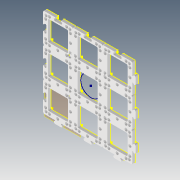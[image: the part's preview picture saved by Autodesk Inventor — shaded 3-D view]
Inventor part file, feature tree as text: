
AUTODESK INVENTOR PART (.ipt)
format: ipt  version: 2022 (Build 260153000, 153)  size: 1,184,256 bytes
history: native  units: mm
features: other x5, sketch x4, extrude x2, reference x2, projected_geometry x2, plane x1, pattern_linear x1, hole x1
ambient origin geometry x8: Origin, YZ Plane, XZ Plane, XY Plane, X Axis, Y Axis, Z Axis, Center Point
bodies: Solid2 (feature_tree)
feature tree (18):
  plane  "Work Plane2"
  extrude  "Extrusion2"  Depth=5.0mm
  pattern_linear  "Rectangular Pattern1"  Spacing1=0.05mm  [1 undecoded]
  extrude  "Extrusion3"  Depth=20.594885mm
  hole  "Hole2"  [1 undecoded]
  sketch  "Skizze6"  dims[d26=0.05mm d27=0.05mm d28=0.05mm d29=0.05mm d30=0.05mm d31=30.0mm d33=50.0mm d34=30.0mm d36=50.0mm d37=5.0mm d38=0.0mm d39=60.0mm d40=60.0mm d41=3.0mm d42=6.0mm d43=6.0mm d44=3.0mm d45=90.0deg d46=8.0mm d47=20.594885mm]
  sketch  "Sketch3"  dims[d21=5.0mm d22=0.0mm d23=0.05mm]
  reference  "Reference47"
  sketch  "Sketch4"  dims[d24=0.05mm]
  projected_geometry  "Projected Loop1"
  sketch  "Sketch5"  dims[d25=0.05mm]
  reference  "Reference48"
  projected_geometry  "Projizierte Kontur2"
  other  "Assembly1"
  other  "10_Base_puzzle_v3:5"
  other  "<userpath>\Dropbox\UC2\02_CAD\INVENTOR\uc2_v3\Assembly_XYTable_Aliepexress.iam"
  other  "Assembly_XYTable_Aliepexress.iam"
  other  "10_Base_puzzle_v3:1"
note: 2 required parameter values undecoded (feature->parameter linkage not recoverable at this tier; creation-order binding heuristic only, values carry confidence <= 0.55)
